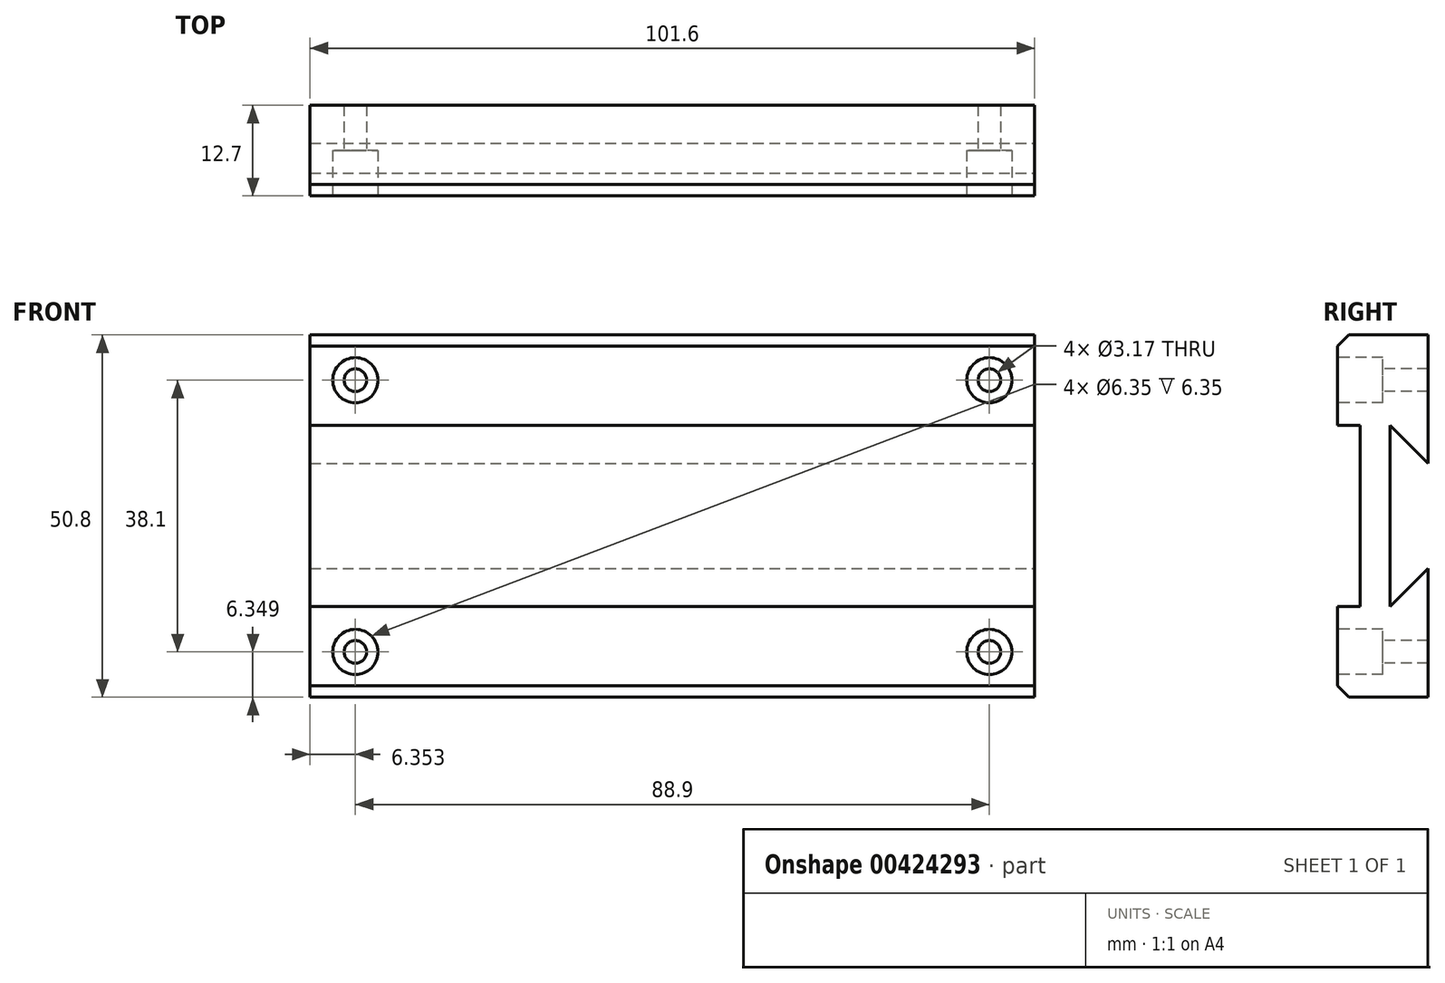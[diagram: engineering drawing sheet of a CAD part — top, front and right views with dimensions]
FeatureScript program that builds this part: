
annotation { "Feature Type Name" : "Feature", "Feature Type Description" : "" }
export const myFeature = defineFeature(function(context is Context, id is Id, definition is map)
    precondition{}
    {
        {
            var Q0;
            Q0=qCreatedBy(makeId("Front.planeOp"),FACE);
            var sketch = newSketch(context, id + "F0", { "sketchPlane" : qUnion([Q0])});
            skLineSegment(sketch, "E0.bottom", {"start": v(-44.44, -21.33) * mm, "end": v(57.16, -21.33) * mm});
            skLineSegment(sketch, "E0.top", {"start": v(-44.44, 29.47) * mm, "end": v(57.16, 29.47) * mm});
            skLineSegment(sketch, "E0.left", {"start": v(-44.44, -21.33) * mm, "end": v(-44.44, 29.47) * mm});
            skLineSegment(sketch, "E0.right", {"start": v(57.16, -21.33) * mm, "end": v(57.16, 29.47) * mm});
            skSolve(sketch);
        }
        {
            var Q0;
            Q0=makeQuery(id+"F0.imprint","IMPRINT",FACE,{"disambiguationData":[TD([[makeQuery(id+"F0.imprint","IMPRINT",EDGE,{"derivedFrom":sQuery(id+"F0.wireOp",EDGE,"E0.bottom")}),1.0]])]});
            extrude(context, id + "F1", {"entities" : qUnion([Q0]), "depth" : 12.7 * mm});
        }
        {
            var Q0;
            Q0=makeQuery(id+"F1.opExtrude","CAP_FACE",FACE,{"disambiguationData":[OSD([sQuery(id+"F0.wireOp",EDGE,"E0.bottom"),sQuery(id+"F0.wireOp",EDGE,"E0.top"),sQuery(id+"F0.wireOp",EDGE,"E0.left"),sQuery(id+"F0.wireOp",EDGE,"E0.right")])],"isStart":false});
            var sketch = newSketch(context, id + "F2", { "sketchPlane" : qUnion([Q0])});
            skPoint(sketch, "E1", {"position": v(-38.09, -14.98) * mm});
            skPoint(sketch, "E2", {"position": v(50.81, -14.98) * mm});
            skPoint(sketch, "E3", {"position": v(-38.09, 23.12) * mm});
            skPoint(sketch, "E4", {"position": v(50.81, 23.12) * mm});
            skSolve(sketch);
        }
        {
            var Q0;
            Q0=sQuery(id+"F2.wireOp",VERTEX,"E1");
            var Q1;
            Q1=sQuery(id+"F2.wireOp",VERTEX,"E2");
            var Q2;
            Q2=sQuery(id+"F2.wireOp",VERTEX,"E4");
            var Q3;
            Q3=sQuery(id+"F2.wireOp",VERTEX,"E3");
            var Q4;
            Q4=makeQuery(id+"F1.opExtrude","SWEPT_BODY",BODY,{"disambiguationData":[OSD([sQuery(id+"F0.wireOp",EDGE,"E0.bottom"),sQuery(id+"F0.wireOp",EDGE,"E0.top"),sQuery(id+"F0.wireOp",EDGE,"E0.left"),sQuery(id+"F0.wireOp",EDGE,"E0.right")])]});
            hole(context, id + "F3", {"style" : HoleStyle.C_BORE, "endStyle" : HoleEndStyle.THROUGH, "holeDiameter" : 3.17 * mm, "cBoreDiameter" : 6.35 * mm, "cBoreDepth" : 6.35 * mm, "isTappedThrough" : true, "tappedDepth" : 12.7 * mm, "tapClearance" : 3, "locations" : qUnion([Q0, Q1, Q2, Q3]), "scope" : qUnion([Q4])});
        }
        {
            var Q0;
            Q0=makeQuery(id+"F1.opExtrude","CAP_FACE",FACE,{"disambiguationData":[OSD([sQuery(id+"F0.wireOp",EDGE,"E0.bottom"),sQuery(id+"F0.wireOp",EDGE,"E0.top"),sQuery(id+"F0.wireOp",EDGE,"E0.left"),sQuery(id+"F0.wireOp",EDGE,"E0.right")])],"isStart":false});
            var sketch = newSketch(context, id + "F4", { "sketchPlane" : qUnion([Q0])});
            skLineSegment(sketch, "E5.bottom", {"start": v(-44.44, -8.63) * mm, "end": v(57.16, -8.63) * mm});
            skLineSegment(sketch, "E5.top", {"start": v(-44.44, 16.77) * mm, "end": v(57.16, 16.77) * mm});
            skLineSegment(sketch, "E5.left", {"start": v(-44.44, -8.63) * mm, "end": v(-44.44, 16.77) * mm});
            skLineSegment(sketch, "E5.right", {"start": v(57.16, -8.63) * mm, "end": v(57.16, 16.77) * mm});
            skSolve(sketch);
        }
        {
            var Q0;
            Q0=makeQuery(id+"F4.imprint","IMPRINT",FACE,{"disambiguationData":[TD([[makeQuery(id+"F4.imprint","IMPRINT",EDGE,{"derivedFrom":sQuery(id+"F4.wireOp",EDGE,"E5.bottom")}),1.0]])]});
            extrude(context, id + "F5", {"entities" : qUnion([Q0]), "operationType" : NewBodyOperationType.REMOVE, "oppositeDirection" : true, "depth" : 3.17 * mm});
        }
        {
            var Q0;
            Q0=makeQuery(id+"F1.opExtrude","CAP_EDGE",EDGE,{"disambiguationData":[OSD([sQuery(id+"F0.wireOp",EDGE,"E0.top")])],"isStart":false});
            var Q1;
            Q1=makeQuery(id+"F1.opExtrude","CAP_EDGE",EDGE,{"disambiguationData":[OSD([sQuery(id+"F0.wireOp",EDGE,"E0.bottom")])],"isStart":false});
            chamfer(context, id + "F6", {"entities" : qUnion([Q0, Q1]), "width" : 1.59 * mm, "tangentPropagation" : true});
        }
        {
            var Q0;
            Q0=makeQuery(id+"F1.opExtrude","SWEPT_FACE",FACE,{"disambiguationData":[OSD([sQuery(id+"F0.wireOp",EDGE,"E0.right")])]});
            var sketch = newSketch(context, id + "F7", { "sketchPlane" : qUnion([Q0])});
            skLineSegment(sketch, "E6", {"start": v(-5.34, -8.63) * mm, "end": v(-5.34, 16.77) * mm});
            skLineSegment(sketch, "E7", {"start": v(-5.34, 16.77) * mm, "end": v(0, 11.43) * mm});
            skLineSegment(sketch, "E8", {"start": v(-5.34, -8.63) * mm, "end": v(0, -3.29) * mm});
            skLineSegment(sketch, "E9", {"start": v(0, 11.43) * mm, "end": v(0, -3.29) * mm});
            skSolve(sketch);
        }
        {
            var Q0;
            Q0=makeQuery(id+"F7.imprint","IMPRINT",FACE,{"disambiguationData":[TD([[makeQuery(id+"F7.imprint","IMPRINT",EDGE,{"derivedFrom":sQuery(id+"F7.wireOp",EDGE,"E6")}),-1.0]])]});
            extrude(context, id + "F8", {"entities" : qUnion([Q0]), "operationType" : NewBodyOperationType.REMOVE, "endBound" : BoundingType.THROUGH_ALL, "oppositeDirection" : true, "depth" : 25.4 * mm});
        }
    });
